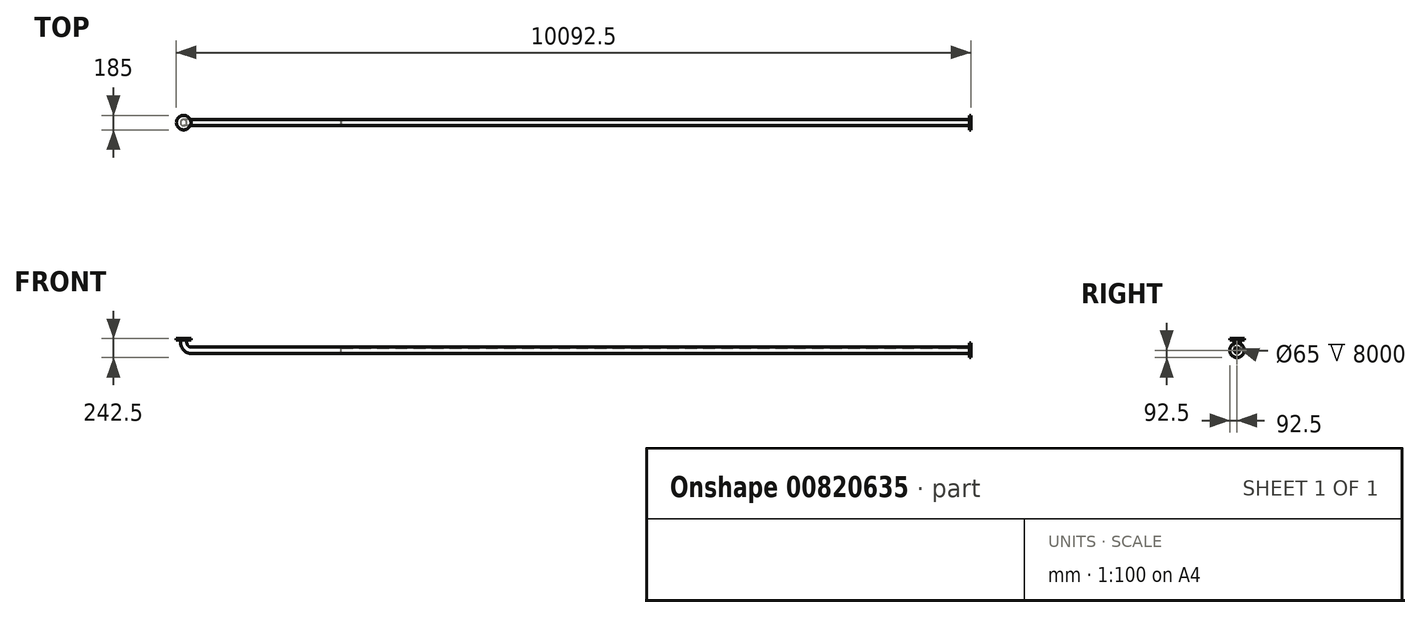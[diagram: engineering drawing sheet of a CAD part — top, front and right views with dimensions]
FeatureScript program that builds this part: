
annotation { "Feature Type Name" : "Feature", "Feature Type Description" : "" }
export const myFeature = defineFeature(function(context is Context, id is Id, definition is map)
    precondition{}
    {
        {
            var Q0;
            Q0=qCreatedBy(makeId("Front.planeOp"),FACE);
            var sketch = newSketch(context, id + "F0", { "sketchPlane" : qUnion([Q0])});
            skLineSegment(sketch, "E0", {"start": v(0, 0) * mm, "end": v(0, -50) * mm});
            skLineSegment(sketch, "E1", {"start": v(100, -150) * mm, "end": v(10000, -150) * mm});
            skPoint(sketch, "E2.visualSharp", {"position": v(0, -150) * mm});
            skArc(sketch, "E2.filletArc", {"start": v(0, -50) * mm, "mid": v(29.29, -120.71) * mm, "end": v(100, -150) * mm});
            skSolve(sketch);
        }
        {
            var Q0;
            Q0=qCreatedBy(makeId("Top.planeOp"),FACE);
            var sketch = newSketch(context, id + "F1", { "sketchPlane" : qUnion([Q0])});
            skCircle(sketch, "E3", {"center": v(0, 0) * mm, "radius": 40 * mm});
            skCircle(sketch, "E4", {"center": v(0, 0) * mm, "radius": 92.5 * mm});
            skSolve(sketch);
        }
        {
            var Q0;
            Q0=makeQuery(id+"F1.imprint","IMPRINT",FACE,{"disambiguationData":[TD([[makeQuery(id+"F1.imprint","IMPRINT",EDGE,{"derivedFrom":sQuery(id+"F1.wireOp",EDGE,"E3")}),-1.0]])]});
            extrude(context, id + "F2", {"entities" : qUnion([Q0]), "oppositeDirection" : true, "depth" : 20 * mm, "offsetDistance" : 25 * mm});
        }
        {
            var Q0;
            Q0=makeQuery(id+"F1.imprint","IMPRINT",FACE,{"disambiguationData":[TD([[makeQuery(id+"F1.imprint","IMPRINT",EDGE,{"derivedFrom":sQuery(id+"F1.wireOp",EDGE,"E3")}),1.0]])]});
            var Q1;
            Q1=sQuery(id+"F0.wireOp",EDGE,"E0");
            var Q2;
            Q2=sQuery(id+"F0.wireOp",EDGE,"E2.filletArc");
            var Q3;
            Q3=sQuery(id+"F0.wireOp",EDGE,"E1");
            sweep(context, id + "F3", {"operationType" : NewBodyOperationType.ADD, "profiles" : qUnion([Q0]), "path" : qUnion([Q1, Q2, Q3])});
        }
        {
            var Q0;
            Q0=makeQuery(id+"F3.opSweep","CAP_FACE",FACE,{"disambiguationData":[OSD([sQuery(id+"F0.wireOp",VERTEX,"E1.end"),sQuery(id+"F1.wireOp",EDGE,"E3")])],"isStart":false});
            var sketch = newSketch(context, id + "F4", { "sketchPlane" : qUnion([Q0])});
            skCircle(sketch, "E5", {"center": v(0, -150) * mm, "radius": 92.5 * mm});
            skSolve(sketch);
        }
        {
            var Q0;
            Q0=makeQuery(id+"F4.imprint","IMPRINT",FACE,{"disambiguationData":[TD([[makeQuery(id+"F4.imprint","IMPRINT",EDGE,{"derivedFrom":sQuery(id+"F4.wireOp",EDGE,"E5")}),1.0]])]});
            extrude(context, id + "F5", {"entities" : qUnion([Q0]), "operationType" : NewBodyOperationType.ADD, "oppositeDirection" : true, "depth" : 20 * mm, "offsetDistance" : 25 * mm});
        }
        {
            var Q0;
            {var subQ0=sQuery(id+"F1.wireOp",EDGE,"E3");var subQ1=sQuery(id+"F0.wireOp",VERTEX,"E1.end");Q0=makeQuery(id+"F5.boolean.opBoolean","MERGE",FACE,{"derivedFrom":[makeQuery(id+"F3.opSweep","CAP_FACE",FACE,{"disambiguationData":[OSD([subQ1,subQ0])],"isStart":false}),makeQuery(id+"F5.opExtrude","CAP_FACE",FACE,{"disambiguationData":[OSD([subQ1,subQ0,sQuery(id+"F4.wireOp",EDGE,"E5")])],"isStart":true})]});}
            var sketch = newSketch(context, id + "F6", { "sketchPlane" : qUnion([Q0])});
            skCircle(sketch, "E6", {"center": v(0, -150) * mm, "radius": 32.5 * mm});
            skSolve(sketch);
        }
        {
            var Q0;
            Q0=makeQuery(id+"F6.imprint","IMPRINT",FACE,{"disambiguationData":[TD([[makeQuery(id+"F6.imprint","IMPRINT",EDGE,{"derivedFrom":sQuery(id+"F6.wireOp",EDGE,"E6")}),1.0]])]});
            extrude(context, id + "F7", {"entities" : qUnion([Q0]), "operationType" : NewBodyOperationType.REMOVE, "oppositeDirection" : true, "depth" : 8000 * mm, "offsetDistance" : 25 * mm});
        }
    });
